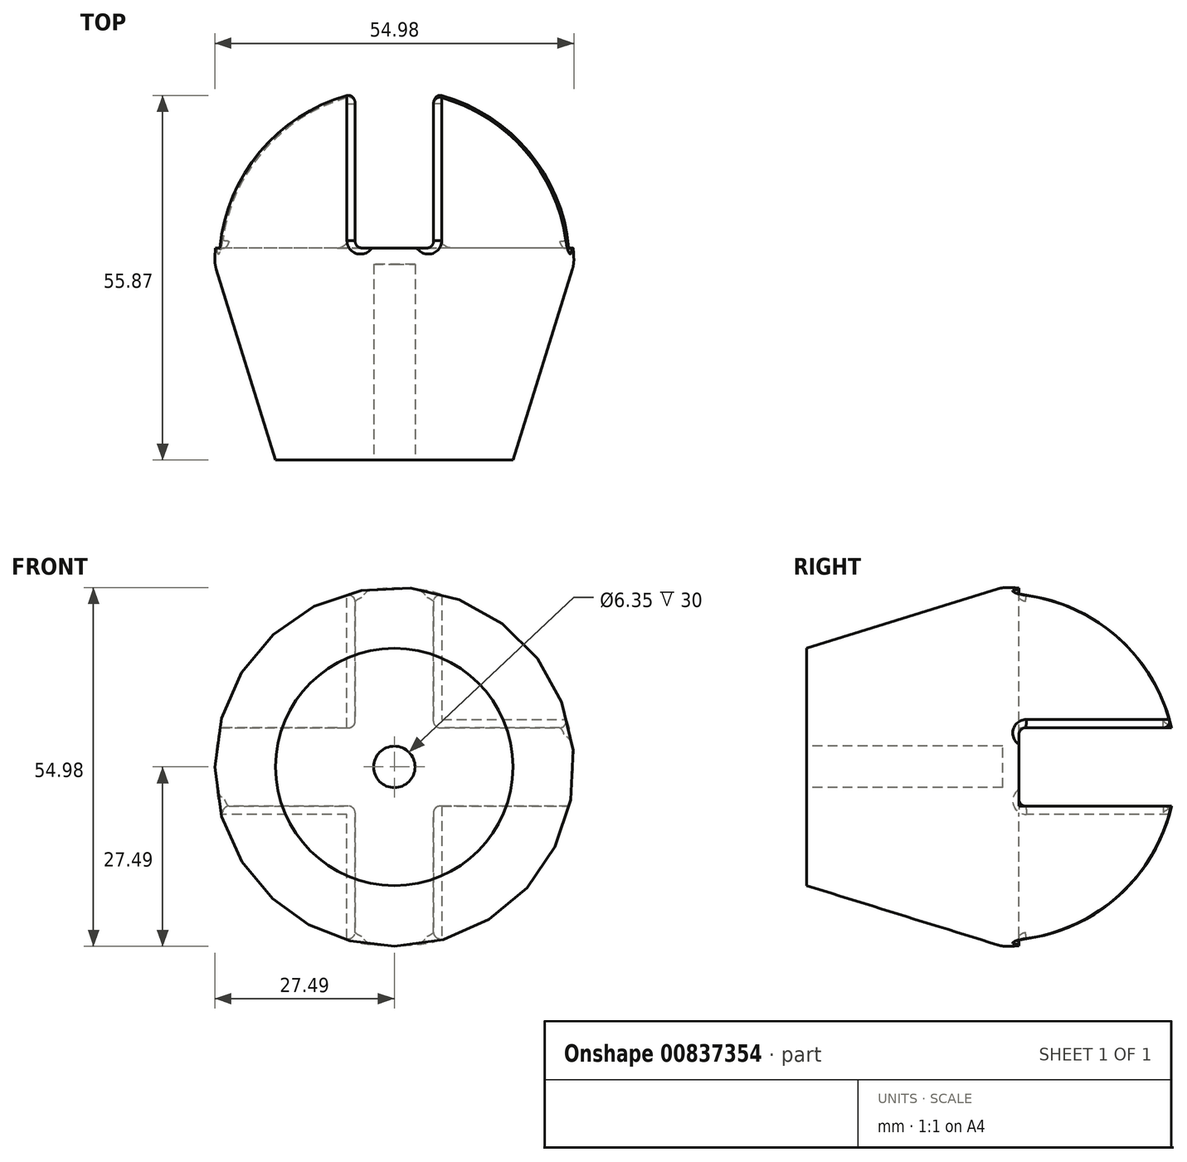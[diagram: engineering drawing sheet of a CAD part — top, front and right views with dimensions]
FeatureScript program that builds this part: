
annotation { "Feature Type Name" : "Feature", "Feature Type Description" : "" }
export const myFeature = defineFeature(function(context is Context, id is Id, definition is map)
    precondition{}
    {
        {
            var Q0;
            Q0=qCreatedBy(makeId("Top.planeOp"),FACE);
            var sketch = newSketch(context, id + "F0", { "sketchPlane" : qUnion([Q0])});
            skArc(sketch, "E0", {"start": v(0, 27.5) * mm, "mid": v(-19.13, 19.75) * mm, "end": v(-27.49, 0.88) * mm});
            skLineSegment(sketch, "E1", {"start": v(-3.17, 0) * mm, "end": v(0, 0) * mm});
            skLineSegment(sketch, "E2", {"start": v(-3.17, 0) * mm, "end": v(-3.17, -30) * mm});
            skLineSegment(sketch, "E3", {"start": v(-3.17, 0) * mm, "end": v(0, 0) * mm, "construction": true});
            skLineSegment(sketch, "E4", {"start": v(-3.18, -30) * mm, "end": v(-18.18, -30) * mm});
            skLineSegment(sketch, "E5", {"start": v(-18.17, -30) * mm, "end": v(-27.26, -0.76) * mm});
            skLineSegment(sketch, "E6", {"start": v(0, 0) * mm, "end": v(0, 27.5) * mm});
            skPoint(sketch, "E7.start.orphan", {"position": v(3.18, -30) * mm});
            skPoint(sketch, "E8.orphan", {"position": v(3.18, 0) * mm});
            skPoint(sketch, "E9.visualSharp", {"position": v(-27.5, 0) * mm});
            skArc(sketch, "E9.filletArc", {"start": v(-27.49, 0.88) * mm, "mid": v(-27.44, 0.05) * mm, "end": v(-27.26, -0.76) * mm});
            skSolve(sketch);
        }
        {
            var Q0;
            Q0 = qSketchRegion(id + "F0", true);
            var Q1;
            Q1=sQuery(id+"F0.wireOp",EDGE,"E6");
            revolve(context, id + "F1", {"surfaceOperationType" : NewSurfaceOperationType.NEW, "entities" : qUnion([Q0]), "axis" : qUnion([Q1]), "revolveType" : RevolveType.FULL});
        }
        {
            var Q0;
            Q0=makeQuery(id+"F1.opRevolve","SWEPT_FACE",FACE,{"disambiguationData":[OSD([sQuery(id+"F0.wireOp",EDGE,"E4")])]});
            cPlane(context, id + "F2", {"entities" : qUnion([Q0]), "cplaneType" : CPlaneType.OFFSET, "offset" : 57.5 * mm, "oppositeDirection" : true, "width" : 150 * mm, "height" : 150 * mm});
        }
        {
            var Q0;
            Q0=qCreatedBy(id+"F2.planeOp",FACE);
            var sketch = newSketch(context, id + "F3", { "sketchPlane" : qUnion([Q0])});
            skCircle(sketch, "E10", {"center": v(0, 0) * mm, "radius": 27.5 * mm});
            skLineSegment(sketch, "E11", {"start": v(26.84, 6) * mm, "end": v(6, 6) * mm});
            skLineSegment(sketch, "E12", {"start": v(26.84, -6) * mm, "end": v(6, -6) * mm});
            skLineSegment(sketch, "E13.1.0", {"start": v(6, -26.84) * mm, "end": v(6, -6) * mm});
            skLineSegment(sketch, "E13.1.1", {"start": v(-6, -26.84) * mm, "end": v(-6, -6) * mm});
            skLineSegment(sketch, "E13.anchor1", {"start": v(0, 0) * mm, "end": v(-26.84, 6) * mm, "construction": true});
            skLineSegment(sketch, "E13.anchor2", {"start": v(0, 0) * mm, "end": v(6, 26.84) * mm, "construction": true});
            skLineSegment(sketch, "E14.trimOffspring", {"start": v(6, 6) * mm, "end": v(6, 26.84) * mm});
            skLineSegment(sketch, "E15.trimOffspring", {"start": v(-6, 6) * mm, "end": v(-26.84, 6) * mm});
            skLineSegment(sketch, "E16.trimOffspring", {"start": v(-6, 6) * mm, "end": v(-6, 26.84) * mm});
            skLineSegment(sketch, "E17.trimOffspring", {"start": v(-6, -6) * mm, "end": v(-26.84, -6) * mm});
            skSolve(sketch);
        }
        {
            var Q0;
            {var subQ4=sQuery(id+"F3.wireOp",EDGE,"E11");Q0=makeQuery(id+"F3.imprint","IMPRINT",FACE,{"disambiguationData":[TD([[makeQuery(id+"F3.imprint","IMPRINT",EDGE,{"derivedFrom":subQ4}),1.0]])]});}
            extrude(context, id + "F4", {"entities" : qUnion([Q0]), "operationType" : NewBodyOperationType.REMOVE, "depth" : 25 * mm, "offsetDistance" : 25 * mm});
        }
        {
            var Q0;
            Q0=makeQuery(id+"F4.boolean.opBoolean","INTERSECT",EDGE,{"derivedFrom":[makeQuery(id+"F1.opRevolve","SWEPT_FACE",FACE,{"disambiguationData":[OSD([sQuery(id+"F0.wireOp",EDGE,"E0")])]}),makeQuery(id+"F4.opExtrude","SWEPT_FACE",FACE,{"disambiguationData":[OSD([sQuery(id+"F3.wireOp",EDGE,"E13.1.0")])]})]});
            var Q1;
            Q1=makeQuery(id+"F4.boolean.opBoolean","COPY",EDGE,{"derivedFrom":makeQuery(id+"F4.opExtrude","SWEPT_EDGE",EDGE,{"disambiguationData":[OSD([sQuery(id+"F3.wireOp",EDGE,"E12"),sQuery(id+"F3.wireOp",EDGE,"E13.1.0")])]})});
            var Q2;
            Q2=makeQuery(id+"F4.boolean.opBoolean","COPY",EDGE,{"derivedFrom":makeQuery(id+"F4.opExtrude","CAP_EDGE",EDGE,{"disambiguationData":[OSD([sQuery(id+"F3.wireOp",EDGE,"E13.1.0")])],"isStart":false})});
            var Q3;
            Q3=makeQuery(id+"F4.boolean.opBoolean","COPY",FACE,{"derivedFrom":makeQuery(id+"F4.opExtrude","SWEPT_FACE",FACE,{"disambiguationData":[OSD([sQuery(id+"F3.wireOp",EDGE,"E14.trimOffspring")])]})});
            var Q4;
            Q4=makeQuery(id+"F4.boolean.opBoolean","COPY",FACE,{"derivedFrom":makeQuery(id+"F4.opExtrude","SWEPT_FACE",FACE,{"disambiguationData":[OSD([sQuery(id+"F3.wireOp",EDGE,"E11")])]})});
            var Q5;
            Q5=makeQuery(id+"F4.boolean.opBoolean","COPY",FACE,{"derivedFrom":makeQuery(id+"F4.opExtrude","SWEPT_FACE",FACE,{"disambiguationData":[OSD([sQuery(id+"F3.wireOp",EDGE,"E13.1.1")])]})});
            var Q6;
            Q6=makeQuery(id+"F4.boolean.opBoolean","COPY",FACE,{"derivedFrom":makeQuery(id+"F4.opExtrude","SWEPT_FACE",FACE,{"disambiguationData":[OSD([sQuery(id+"F3.wireOp",EDGE,"E16.trimOffspring")])]})});
            var Q7;
            Q7=makeQuery(id+"F4.boolean.opBoolean","COPY",FACE,{"derivedFrom":makeQuery(id+"F4.opExtrude","SWEPT_FACE",FACE,{"disambiguationData":[OSD([sQuery(id+"F3.wireOp",EDGE,"E17.trimOffspring")])]})});
            fillet(context, id + "F5", {"entities" : qUnion([Q0, Q1, Q2, Q3, Q4, Q5, Q6, Q7]), "radius" : 1 * mm, "tangentPropagation" : true, "allowEdgeOverflow" : false});
        }
    });
